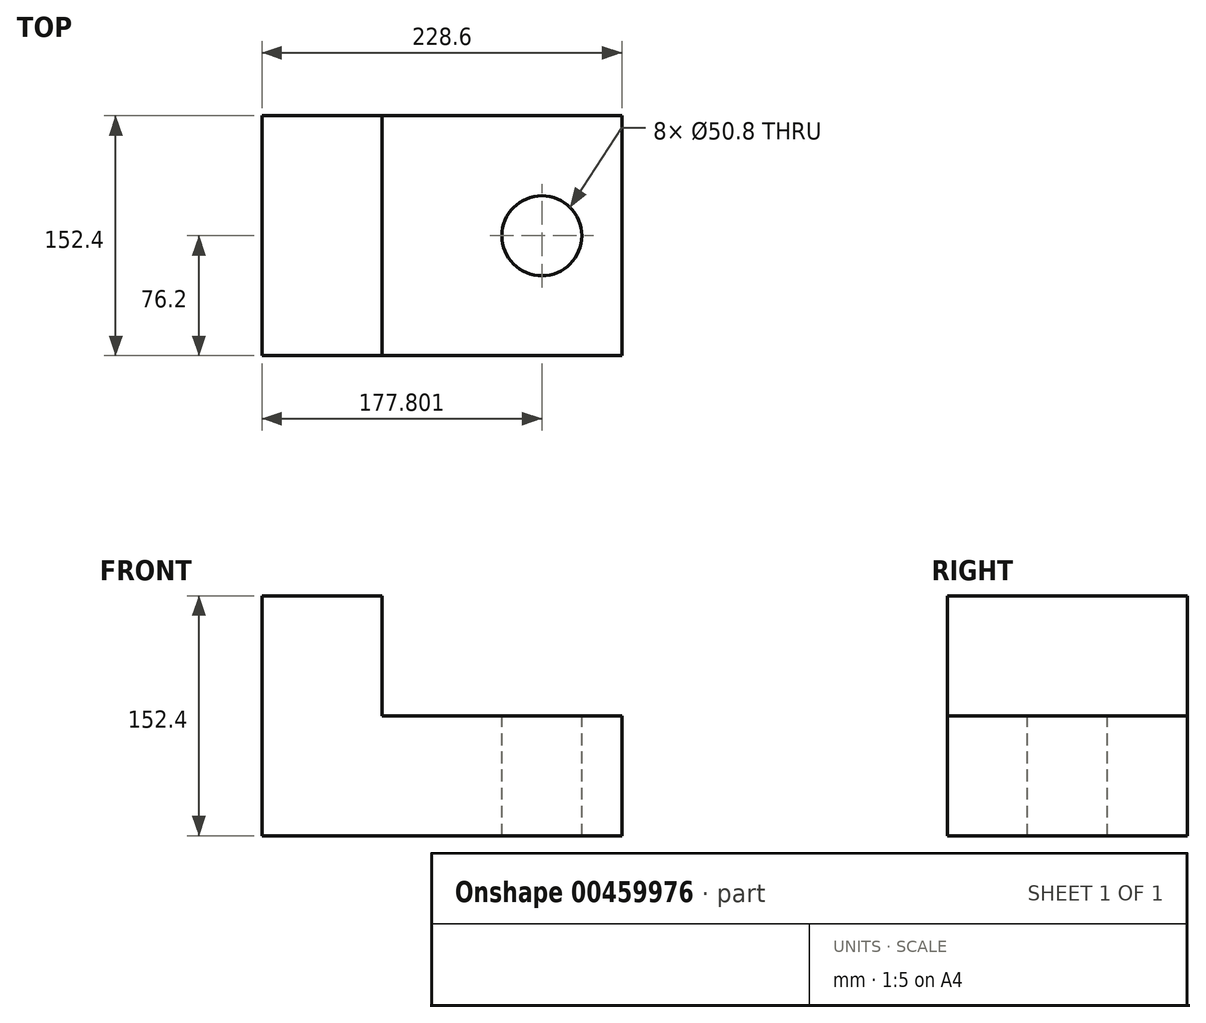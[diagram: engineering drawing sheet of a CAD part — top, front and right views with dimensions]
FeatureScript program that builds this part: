
annotation { "Feature Type Name" : "Feature", "Feature Type Description" : "" }
export const myFeature = defineFeature(function(context is Context, id is Id, definition is map)
    precondition{}
    {
        {
            var Q0;
            Q0=qCreatedBy(makeId("Front.planeOp"),FACE);
            var sketch = newSketch(context, id + "F0", { "sketchPlane" : qUnion([Q0])});
            skLineSegment(sketch, "E0", {"start": v(-198.85, 0) * mm, "end": v(-198.85, 152.4) * mm});
            skLineSegment(sketch, "E1", {"start": v(-198.85, 152.4) * mm, "end": v(-122.65, 152.4) * mm});
            skLineSegment(sketch, "E2", {"start": v(-122.65, 152.4) * mm, "end": v(-122.65, 76.2) * mm});
            skLineSegment(sketch, "E3", {"start": v(-122.65, 76.2) * mm, "end": v(29.75, 76.2) * mm});
            skLineSegment(sketch, "E4", {"start": v(29.75, 76.2) * mm, "end": v(29.75, 0) * mm});
            skLineSegment(sketch, "E5", {"start": v(29.75, 0) * mm, "end": v(-198.85, 0) * mm});
            skSolve(sketch);
        }
        {
            var Q0;
            Q0 = qSketchRegion(id + "F0", true);
            extrude(context, id + "F1", {"entities" : qUnion([Q0]), "depth" : 152.4 * mm});
        }
        {
            var Q0;
            Q0=makeQuery(id+"F1.opExtrude","SWEPT_FACE",FACE,{"disambiguationData":[OSD([sQuery(id+"F0.wireOp",EDGE,"E3")])]});
            var sketch = newSketch(context, id + "F2", { "sketchPlane" : qUnion([Q0])});
            skCircle(sketch, "E6", {"center": v(-21.05, -76.2) * mm, "radius": 25.4 * mm});
            skSolve(sketch);
        }
        {
            var Q0;
            Q0 = qSketchRegion(id + "F2", true);
            extrude(context, id + "F3", {"entities" : qUnion([Q0]), "operationType" : NewBodyOperationType.REMOVE, "oppositeDirection" : true, "depth" : 76.2 * mm});
        }
    });
